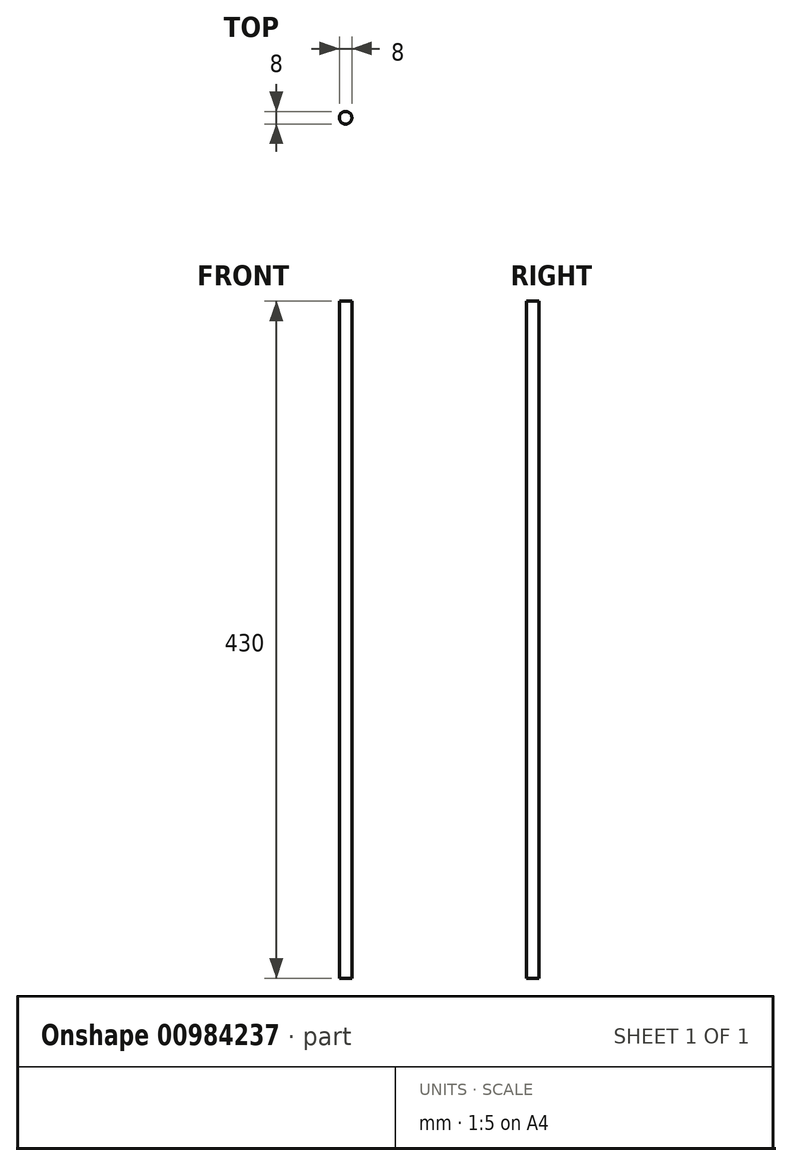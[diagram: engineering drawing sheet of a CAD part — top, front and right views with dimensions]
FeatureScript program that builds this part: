
annotation { "Feature Type Name" : "Feature", "Feature Type Description" : "" }
export const myFeature = defineFeature(function(context is Context, id is Id, definition is map)
    precondition{}
    {
        {
            var Q0;
            Q0=qCreatedBy(makeId("Top.planeOp"),FACE);
            var sketch = newSketch(context, id + "F0", { "sketchPlane" : qUnion([Q0])});
            skCircle(sketch, "E0", {"center": v(0, 0) * mm, "radius": 4 * mm});
            skSolve(sketch);
        }
        {
            var Q0;
            Q0=makeQuery(id+"F0.imprint","IMPRINT",FACE,{"disambiguationData":[TD([[makeQuery(id+"F0.imprint","IMPRINT",EDGE,{"derivedFrom":sQuery(id+"F0.wireOp",EDGE,"E0")}),1.0]])]});
            extrude(context, id + "F1", {"entities" : qUnion([Q0]), "oppositeDirection" : true, "depth" : 430 * mm, "offsetDistance" : 25 * mm});
        }
    });
